# Revit family: Калитка_PROM BARS_H1300-2500
name_source: partatom
category: Специальное оборудование
units: mm (PartAtom-declared; Revit-internal decimal feet)

## family parameters
Всегда вертикально = Да
На основе рабочей плоскости = Нет
Общий = Нет
При загрузке вырезать с полостями = Нет
Размер круглого соединителя = Использовать диаметр
Тип детали = Нормальный
Точка расчета площади = Нет

## types (8) — shared parameters
ADSK_Единица измерения = шт.
ADSK_Завод-изготовитель = FENSYS
ADSK_Комплект = Калитка
URL = https://www.fensys.ru
Изготовитель = FENSYS
Материал_Сетка = FENSYS_Рейка
Материал_Столбы = FENSYS_Столб
Ширина рамки = 60 мм

## per-type parameters (varying)
| type | ADSK_Обозначение | PROM 2 P2B | PROM PB | PROM_Н | Бетонирование в кондукторе | Бетонирование столбы (SI) | Высота Замка | Глубина столба | Тип креплния | Фланец | Фланец под винтовую опору |
| PROM BARS PB_Фланец под винтовую опору | PROM BARS/SITgs | Нет | Да | PROM_BARS | Нет | Нет | 1040 мм | 0 мм | 4 | Нет | Да |
| PROM BARS PB_Фланец | PROM BARS/SIT | Нет | Да | PROM_BARS | Нет | Нет | 1040 мм | 0 мм | 3 | Да | Нет |
| PROM2 BARS P2B_Фланец | PROM2 BARS/SIT | Да | Нет | PROM2_BARS | Нет | Нет | 1040 мм | 0 мм | 3 | Да | Нет |
| PROM2 BARS P2B_Фланец под винтовую опору | PROM2 BARS/SITgs | Да | Нет | PROM2_BARS | Нет | Нет | 1040 мм | 0 мм | 4 | Нет | Да |
| PROM2 BARS P2B_Бетонирование в кондукторе | PROM2 BARS/SIC | Да | Нет | PROM2_BARS | Да | Нет | 1040 мм | 500 мм | 1 | Нет | Нет |
| PROM BARS PB_Бетонирование в кондукторе | PROM BARS/SIC | Нет | Да | PROM_BARS | Да | Нет | 1050 мм | 500 мм | 1 | Нет | Нет |
| PROM BARS PB_Бетонирование столбы (SI) | PROM BARS/SI | Нет | Да | PROM_BARS | Нет | Да | 1040 мм | 500 мм | 2 | Нет | Нет |
| PROM2 BARS P2B_Бетонирование столбы (SI) | PROM2 BARS/SI | Да | Нет | PROM2_BARS | Нет | Да | 1040 мм | 500 мм | 2 | Нет | Нет |
